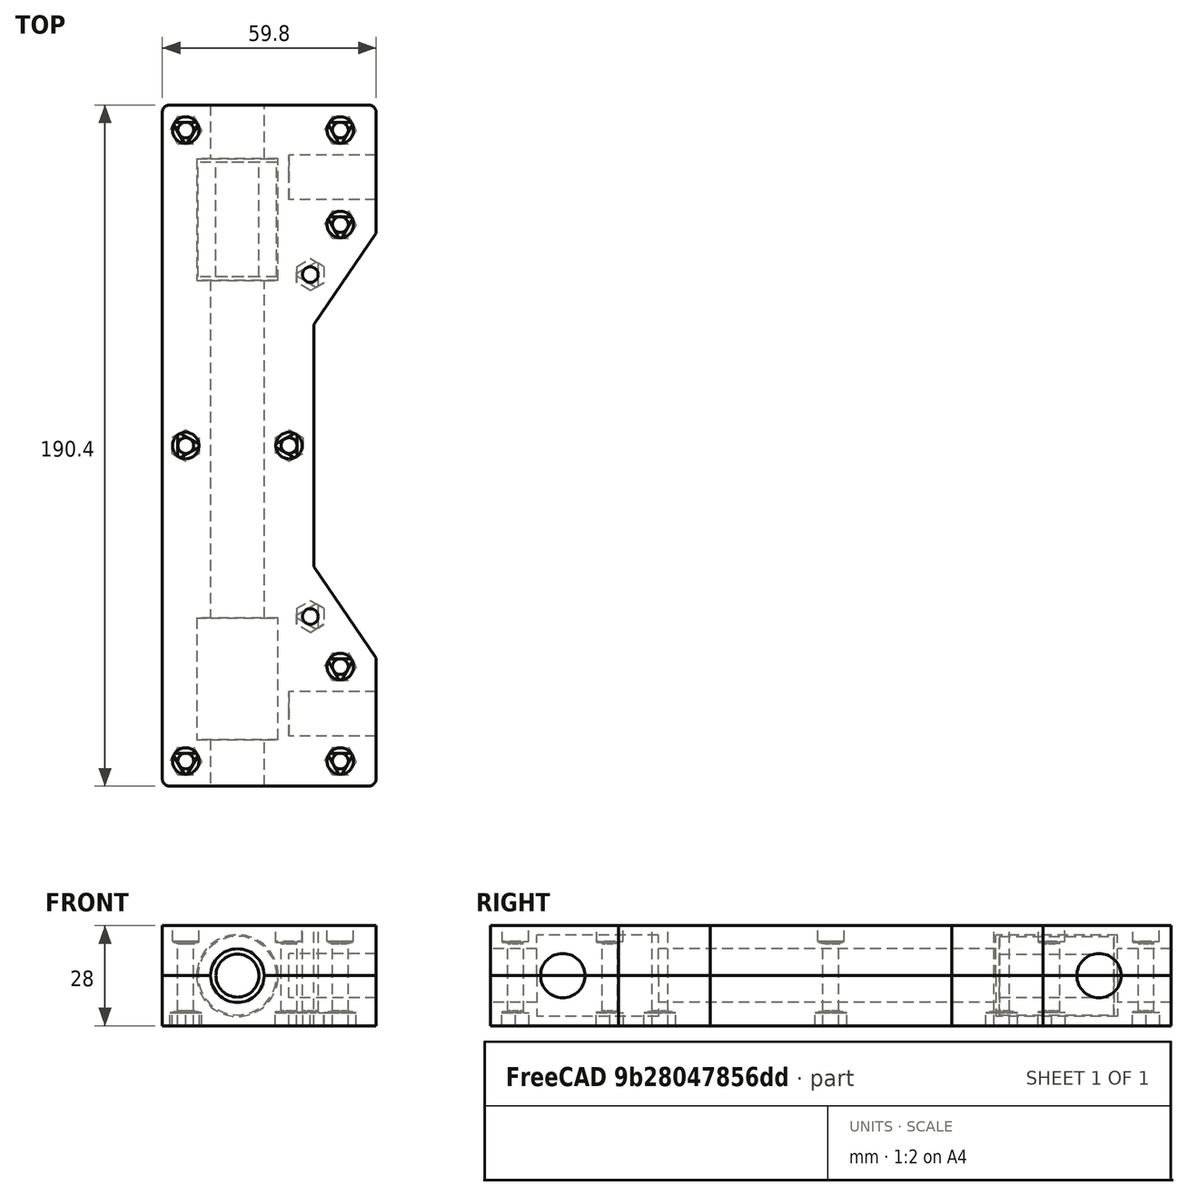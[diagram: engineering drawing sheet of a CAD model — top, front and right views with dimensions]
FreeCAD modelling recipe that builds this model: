
FCSTD DOCUMENT  (FreeCAD 0.16R6706 (Git))
Label: xend_shaft_slider
License: All rights reserved
LicenseURL: http://en.wikipedia.org/wiki/All_rights_reserved
objects: Part::FeaturePython×10, Part::Prism×10, Part::Cylinder×6, Part::Extrusion×5, Part::Circle×4, Part::MultiFuse×4, Part::Cut×3, Part::Common×3, Part::Box×2, Part::Fillet×2, Part::Polygon×1
note: 50 computed .brp shape members not serialized (recipe doc carries the construction recipe); baked Part::Feature solids carry a one-line shape summary decoded from their .brp

FEATURE [Part::Box] todslid_box
  Height = 14
  Length = 59.8
  Placement = pos=(-21,-95.2,0) rot=(0,0,1;0rad)
  Width = 190.4
FEATURE [Part::Box] botslid_box
  Height = 14
  Length = 59.8
  Placement = pos=(-21,-95.2,-14) rot=(0,0,1;0rad)
  Width = 190.4
FEATURE [Part::Fillet] topslid_chf
  Base = -> todslid_box
  Edges = 4 edges r=2: [Edge1,Edge3,Edge5,Edge7]
FEATURE [Part::Fillet] botslid_chf
  Base = -> botslid_box
  Edges = 4 edges r=2: [Edge1,Edge3,Edge5,Edge7]
FEATURE [Part::Circle] sliderod_circ
  Angle0 = 0
  Angle1 = 360
  Placement = pos=(0,-96.2,0) rot=(-1,0,0;1.5708rad)
  Radius = 7.5
FEATURE [Part::Extrusion] sliderod
  Base = -> sliderod_circ
  Dir = (0,192.4,0)
  Solid = true
FEATURE [Part::Cylinder] lm12uu_0_ext
  Angle = 360
  Height = 32
  Placement = pos=(0,-81.2,0) rot=(-1,0,0;1.5708rad)
  Radius = 11
FEATURE [Part::Cylinder] lm12uu_0_int
  Angle = 360
  Height = 34
  Placement = pos=(0,-82.2,0) rot=(-1,0,0;1.5708rad)
  Radius = 6
FEATURE [Part::Cut] lm12uu_0
  Base = -> lm12uu_0_ext
  Tool = -> lm12uu_0_int
FEATURE [Part::Circle] lm12uu_0_cont_circ
  Angle0 = 0
  Angle1 = 360
  Placement = pos=(0,-82.2,0) rot=(-1,0,0;1.5708rad)
  Radius = 11.4
FEATURE [Part::Extrusion] lm12uu_0_cont
  Base = -> lm12uu_0_cont_circ
  Dir = (0,34,0)
  Solid = true
FEATURE [Part::FeaturePython] Clone  label="lm12uu_001"  # Draft clone (typed FeaturePython)
  Objects = -> [lm12uu_0]
  Placement = pos=(0,128.4,0) rot=(0,0,1;0rad)
  Scale = (1,1,1)
FEATURE [Part::FeaturePython] Clone001  label="lm12uu_0_cont001"  # Draft clone (typed FeaturePython)
  Objects = -> [lm12uu_0_cont]
  Placement = pos=(0,128.4,0) rot=(0,0,1;0rad)
  Scale = (1,1,1)
FEATURE [Part::Circle] holdrod_0_circ
  Angle0 = 0
  Angle1 = 360
  Placement = pos=(14.4,0,0) rot=(0,1,0;1.5708rad)
  Radius = 6.2
FEATURE [Part::Extrusion] holdrod_0
  Base = -> holdrod_0_circ
  Dir = (25,0,0)
  Placement = pos=(0,-75,0) rot=(0,0,1;0rad)
  Solid = true
FEATURE [Part::Circle] holdrod_1_circ
  Angle0 = 0
  Angle1 = 360
  Placement = pos=(14.4,0,0) rot=(0,1,0;1.5708rad)
  Radius = 6.2
FEATURE [Part::Extrusion] holdrod_1
  Base = -> holdrod_1_circ
  Dir = (25,0,0)
  Placement = pos=(0,75,0) rot=(0,0,1;0rad)
  Solid = true
FEATURE [Part::Cylinder] bolt_hole_bolt_shank
  Angle = 360
  Height = 30
  Placement = pos=(0,0,-1) rot=(0,0,1;0rad)
  Radius = 2.2
FEATURE [Part::Cylinder] bolt_hole_bolt_head
  Angle = 360
  Height = 5.4
  Placement = pos=(0,0,23.6) rot=(0,0,1;0rad)
  Radius = 3.7
FEATURE [Part::Prism] bolt_hole_bolt_sup1
  Circumradius = 4.4
  Height = 4.7
  Placement = pos=(0,0,23.3) rot=(0,0,1;0.523599rad)
  Polygon = 3
FEATURE [Part::Cylinder] bolt_hole_bolt_sup1away
  Angle = 360
  Height = 4.7
  Placement = pos=(0,0,23.3) rot=(0,0,1;0rad)
  Radius = 3.7
FEATURE [Part::Common] sup1cut
  Base = -> bolt_hole_bolt_sup1
  Tool = -> bolt_hole_bolt_sup1away
FEATURE [Part::Prism] bolt_hole_bolt_sup2
  Circumradius = 2.53
  Height = 5
  Placement = pos=(0,0,23) rot=(0,0,1;0rad)
  Polygon = 6
FEATURE [Part::MultiFuse] bolt_hole_bolt
  Shapes = -> [bolt_hole_bolt_shank,bolt_hole_bolt_head,sup1cut,bolt_hole_bolt_sup2]
FEATURE [Part::Prism] bolt_hole_nut
  Circumradius = 4.43
  Height = 4.6
  Placement = pos=(0,0,-1) rot=(0,0,1;0rad)
  Polygon = 6
FEATURE [Part::Prism] bolt_hole_nutsup1
  Circumradius = 4.4
  Height = 3.9
  Placement = pos=(0,0,0) rot=(0,0,1;0.523599rad)
  Polygon = 3
FEATURE [Part::Prism] bolt_hole_supnut1away
  Circumradius = 4.43
  Height = 3.9
  Polygon = 6
FEATURE [Part::Common] supnut1_cut
  Base = -> bolt_hole_nutsup1
  Tool = -> bolt_hole_supnut1away
FEATURE [Part::Prism] bolt_hole_supnut2
  Circumradius = 2.53
  Height = 4.2
  Polygon = 6
FEATURE [Part::MultiFuse] boltnut
  Placement = pos=(-14.45,0,-14) rot=(0,0,1;1.5708rad)
  Shapes = -> [bolt_hole_bolt,bolt_hole_nut,supnut1_cut,bolt_hole_supnut2]
FEATURE [Part::FeaturePython] Clone002  label="bolt_hole_r"  # Draft clone (typed FeaturePython)
  Objects = -> [boltnut]
  Placement = pos=(14.45,0,-14) rot=(0,0,1;0.523599rad)
  Scale = (1,1,1)
FEATURE [Part::FeaturePython] Clone003  label="bolt_hole_lu"  # Draft clone (typed FeaturePython)
  Objects = -> [boltnut]
  Placement = pos=(-14.45,-88.2,-14) rot=(0,0,1;0rad)
  Scale = (1,1,1)
FEATURE [Part::FeaturePython] Clone004  label="bolt_hole_ld"  # Draft clone (typed FeaturePython)
  Objects = -> [boltnut]
  Placement = pos=(-14.45,88.2,-14) rot=(0,0,1;0rad)
  Scale = (1,1,1)
FEATURE [Part::FeaturePython] Clone005  label="bolt_hole_ru"  # Draft clone (typed FeaturePython)
  Objects = -> [boltnut]
  Placement = pos=(28.8,88.2,-14) rot=(0,0,1;0rad)
  Scale = (1,1,1)
FEATURE [Part::FeaturePython] Clone006  label="bolt_hole_rd"  # Draft clone (typed FeaturePython)
  Objects = -> [boltnut]
  Placement = pos=(28.8,-88.2,-14) rot=(0,0,1;0rad)
  Scale = (1,1,1)
FEATURE [Part::FeaturePython] Clone007  label="bolt_hole_rmu"  # Draft clone (typed FeaturePython)
  Objects = -> [boltnut]
  Placement = pos=(28.8,61.8,-14) rot=(0,0,1;0rad)
  Scale = (1,1,1)
FEATURE [Part::FeaturePython] Clone008  label="bolt_hole_rmd"  # Draft clone (typed FeaturePython)
  Objects = -> [boltnut]
  Placement = pos=(28.8,-61.8,-14) rot=(0,0,1;0rad)
  Scale = (1,1,1)
FEATURE [Part::Cylinder] boltpul_hole_shank
  Angle = 360
  Height = 30
  Placement = pos=(0,0,-1) rot=(0,0,1;0rad)
  Radius = 2.2
FEATURE [Part::Prism] boltpul_hole_head
  Circumradius = 4.43
  Height = 4.6
  Placement = pos=(0,0,-1) rot=(0,0,1;0rad)
  Polygon = 6
FEATURE [Part::Prism] boltpul_hole_sup1
  Circumradius = 4.4
  Height = 3.9
  Placement = pos=(0,0,0) rot=(0,0,1;0.523599rad)
  Polygon = 3
FEATURE [Part::Prism] boltpul_hole_sup1away
  Circumradius = 4.43
  Height = 3.9
  Polygon = 6
FEATURE [Part::Common] sup1cut001
  Base = -> boltpul_hole_sup1
  Tool = -> boltpul_hole_sup1away
FEATURE [Part::Prism] boltpul_hole_sup2
  Circumradius = 2.53
  Height = 4.2
  Polygon = 6
FEATURE [Part::MultiFuse] boltpul_hole
  Placement = pos=(20.4,47.8,-14) rot=(0,0,1;0.523599rad)
  Shapes = -> [boltpul_hole_shank,boltpul_hole_head,sup1cut001,boltpul_hole_sup2]
FEATURE [Part::FeaturePython] Clone009  label="boltpul_hole_1"  # Draft clone (typed FeaturePython)
  Objects = -> [boltpul_hole]
  Placement = pos=(20.4,-47.8,-14) rot=(0,0,1;0.523599rad)
  Scale = (1,1,1)
FEATURE [Part::Polygon] dent_plane
  Close = true
  Nodes = (4) [(39.8,60.8,-15),(21.4,33.8,-15),(21.4,-33.8,-15),(39.8,-60.8,-15)]
FEATURE [Part::Extrusion] dent
  Base = -> dent_plane
  Dir = (0,0,30)
  Solid = true
FEATURE [Part::MultiFuse] holes
  Shapes = -> [sliderod,lm12uu_0_cont,Clone001,holdrod_0,holdrod_1,boltnut,Clone002,Clone003,Clone004,Clone005,Clone006,Clone007,Clone008,boltpul_hole,Clone009,dent]
FEATURE [Part::Cut] top_slide
  Base = -> topslid_chf
  Tool = -> holes
FEATURE [Part::Cut] bot_slide
  Base = -> botslid_chf
  Tool = -> holes
